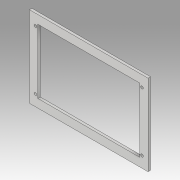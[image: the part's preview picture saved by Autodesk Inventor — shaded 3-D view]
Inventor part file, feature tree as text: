
AUTODESK INVENTOR PART (.ipt)
format: ipt  version: 2019.3 (Build 233278000, 278)  size: 104,448 bytes
history: native  units: mm
features: extrude x1, sketch x1
ambient origin geometry x8: Origin, YZ Plane, XZ Plane, XY Plane, X Axis, Y Axis, Z Axis, Center Point
bodies: Solid1 (feature_tree)
feature tree (2):
  extrude  "Extrusion1"  Depth=77.0mm
  sketch  "Sketch1"  dims[d0=122.0mm d1=77.0mm d2=10.0mm d3=10.0mm d4=10.0mm d5=10.0mm d6=3.1mm d7=127.6mm d8=63.8mm d9=70.6mm d10=3.2mm d11=3.2mm d12=3.0mm d13=0.0mm]
